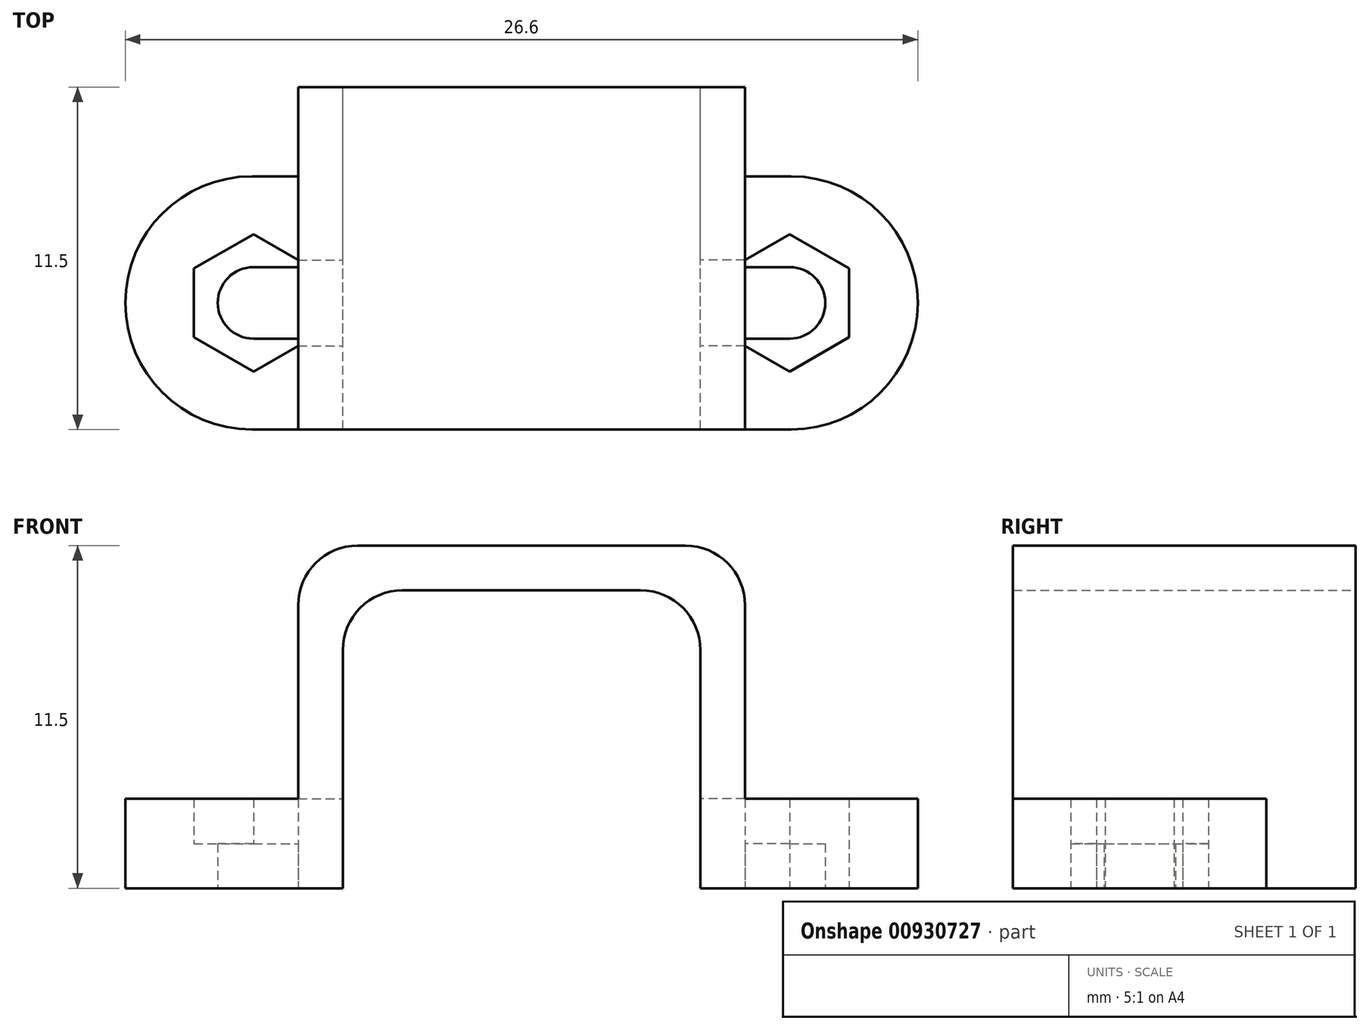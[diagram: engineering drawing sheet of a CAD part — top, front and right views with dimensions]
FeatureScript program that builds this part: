
annotation { "Feature Type Name" : "Feature", "Feature Type Description" : "" }
export const myFeature = defineFeature(function(context is Context, id is Id, definition is map)
    precondition{}
    {
        {
            var Q0;
            Q0=qCreatedBy(makeId("Top.planeOp"),FACE);
            var sketch = newSketch(context, id + "F0", { "sketchPlane" : qUnion([Q0])});
            skLineSegment(sketch, "E0", {"start": v(0, 0) * mm, "end": v(-9, 0) * mm, "construction": true});
            skArc(sketch, "E1", {"start": v(-9, 1.2) * mm, "mid": v(-10.2, 0) * mm, "end": v(-9, -1.2) * mm});
            skCircle(sketch, "E2.cCircle", {"center": v(-9, 0) * mm, "radius": 2 * mm, "construction": true});
            skLineSegment(sketch, "E2.2", {"start": v(-9, -2.3) * mm, "end": v(-11, -1.15) * mm});
            skLineSegment(sketch, "E2.3", {"start": v(-11, -1.15) * mm, "end": v(-11, 1.15) * mm});
            skLineSegment(sketch, "E2.4", {"start": v(-11, 1.15) * mm, "end": v(-9, 2.3) * mm});
            skLineSegment(sketch, "E2.5", {"start": v(-9, 2.3) * mm, "end": v(-7.5, 1.44) * mm});
            skPoint(sketch, "E2.0.midPoint", {"position": v(-7, 0) * mm});
            skLineSegment(sketch, "E3", {"start": v(0, -4.25) * mm, "end": v(-7.5, -4.25) * mm});
            skLineSegment(sketch, "E4", {"start": v(-7.5, -4.25) * mm, "end": v(-13.3, -4.25) * mm});
            skLineSegment(sketch, "E5", {"start": v(-13.3, -4.25) * mm, "end": v(-13.3, 4.25) * mm});
            skLineSegment(sketch, "E6", {"start": v(0, -4.25) * mm, "end": v(0, 7.25) * mm});
            skLineSegment(sketch, "E7", {"start": v(-7.5, -4.25) * mm, "end": v(-7.5, 7.25) * mm});
            skLineSegment(sketch, "E8", {"start": v(0, 7.25) * mm, "end": v(-7.5, 7.25) * mm});
            skLineSegment(sketch, "E9", {"start": v(-13.3, 4.25) * mm, "end": v(-7.5, 4.25) * mm});
            skLineSegment(sketch, "E10", {"start": v(-6, -4.25) * mm, "end": v(-6, 7.25) * mm});
            skPoint(sketch, "E11.trimOffspring.end.orphan", {"position": v(-7, 1.15) * mm});
            skLineSegment(sketch, "E12.trimOffspring", {"start": v(-7.5, -1.44) * mm, "end": v(-9, -2.3) * mm});
            skPoint(sketch, "E2.0.end.orphan", {"position": v(-7, -1.15) * mm});
            skPoint(sketch, "E13.start.orphan", {"position": v(-9, -1.2) * mm});
            skLineSegment(sketch, "E14", {"start": v(-7.5, 1.44) * mm, "end": v(-6, 1.44) * mm});
            skLineSegment(sketch, "E15", {"start": v(-7.5, -1.44) * mm, "end": v(-6, -1.44) * mm});
            skPoint(sketch, "E16.start.orphan", {"position": v(-9, 1.2) * mm});
            skLineSegment(sketch, "E17", {"start": v(-9, -1.2) * mm, "end": v(-7.5, -1.2) * mm});
            skLineSegment(sketch, "E18", {"start": v(-9, 1.2) * mm, "end": v(-7.5, 1.2) * mm});
            skLineSegment(sketch, "E19.MirrorCS", {"start": v(0, 7.25) * mm, "end": v(7.5, 7.25) * mm});
            skLineSegment(sketch, "E20.MirrorCS", {"start": v(0, -4.25) * mm, "end": v(7.5, -4.25) * mm});
            skLineSegment(sketch, "E21.MirrorCS", {"start": v(13.3, 4.25) * mm, "end": v(7.5, 4.25) * mm});
            skLineSegment(sketch, "E22.MirrorCS", {"start": v(6, -4.25) * mm, "end": v(6, 7.25) * mm});
            skLineSegment(sketch, "E23.MirrorCS", {"start": v(13.3, -4.25) * mm, "end": v(13.3, 4.25) * mm});
            skLineSegment(sketch, "E24.MirrorCS", {"start": v(7.5, -4.25) * mm, "end": v(13.3, -4.25) * mm});
            skLineSegment(sketch, "E25.MirrorCS", {"start": v(7.5, -4.25) * mm, "end": v(7.5, 7.25) * mm});
            skArc(sketch, "E26.MirrorCS", {"start": v(9, 1.2) * mm, "mid": v(10.2, 0) * mm, "end": v(9, -1.2) * mm});
            skLineSegment(sketch, "E27.MirrorCS", {"start": v(9, -1.2) * mm, "end": v(7.5, -1.2) * mm});
            skLineSegment(sketch, "E28.MirrorCS", {"start": v(9, 1.2) * mm, "end": v(7.5, 1.2) * mm});
            skLineSegment(sketch, "E29.MirrorCS", {"start": v(7.5, 1.44) * mm, "end": v(6, 1.44) * mm});
            skLineSegment(sketch, "E30.MirrorCS", {"start": v(7.5, -1.44) * mm, "end": v(6, -1.44) * mm});
            skLineSegment(sketch, "E31.MirrorCS", {"start": v(9, 2.3) * mm, "end": v(7.5, 1.44) * mm});
            skLineSegment(sketch, "E32.MirrorCS", {"start": v(11, 1.15) * mm, "end": v(9, 2.3) * mm});
            skLineSegment(sketch, "E33.MirrorCS", {"start": v(11, -1.15) * mm, "end": v(11, 1.15) * mm});
            skLineSegment(sketch, "E34.MirrorCS", {"start": v(9, -2.3) * mm, "end": v(11, -1.15) * mm});
            skLineSegment(sketch, "E35.MirrorCS", {"start": v(7.5, -1.44) * mm, "end": v(9, -2.3) * mm});
            skSolve(sketch);
        }
        {
            var Q0;
            {var subQ1=sQuery(id+"F0.wireOp",EDGE,"E6");Q0=makeQuery(id+"F0.imprint","IMPRINT",FACE,{"disambiguationData":[TD([[makeQuery(id+"F0.imprint","IMPRINT",EDGE,{"derivedFrom":subQ1}),1.0]])]});}
            var Q1;
            {var subQ3=sQuery(id+"F0.wireOp",EDGE,"E14");Q1=makeQuery(id+"F0.imprint","IMPRINT",FACE,{"disambiguationData":[TD([[makeQuery(id+"F0.imprint","IMPRINT",EDGE,{"derivedFrom":subQ3}),1.0]])]});}
            var Q2;
            {var subQ0=sQuery(id+"F0.wireOp",EDGE,"E14");Q2=makeQuery(id+"F0.imprint","IMPRINT",FACE,{"disambiguationData":[TD([[makeQuery(id+"F0.imprint","IMPRINT",EDGE,{"derivedFrom":subQ0}),-1.0]])]});}
            var Q3;
            {var subQ5=sQuery(id+"F0.wireOp",EDGE,"E15");Q3=makeQuery(id+"F0.imprint","IMPRINT",FACE,{"disambiguationData":[TD([[makeQuery(id+"F0.imprint","IMPRINT",EDGE,{"derivedFrom":subQ5}),-1.0]])]});}
            var Q4;
            {var subQ5=sQuery(id+"F0.wireOp",EDGE,"E6");Q4=makeQuery(id+"F0.imprint","IMPRINT",FACE,{"disambiguationData":[TD([[makeQuery(id+"F0.imprint","IMPRINT",EDGE,{"derivedFrom":subQ5}),-1.0]])]});}
            var Q5;
            {var subQ4=sQuery(id+"F0.wireOp",EDGE,"E29.MirrorCS");Q5=makeQuery(id+"F0.imprint","IMPRINT",FACE,{"disambiguationData":[TD([[makeQuery(id+"F0.imprint","IMPRINT",EDGE,{"derivedFrom":subQ4}),-1.0]])]});}
            var Q6;
            {var subQ4=sQuery(id+"F0.wireOp",EDGE,"E30.MirrorCS");Q6=makeQuery(id+"F0.imprint","IMPRINT",FACE,{"disambiguationData":[TD([[makeQuery(id+"F0.imprint","IMPRINT",EDGE,{"derivedFrom":subQ4}),-1.0]])]});}
            var Q7;
            {var subQ5=sQuery(id+"F0.wireOp",EDGE,"E30.MirrorCS");Q7=makeQuery(id+"F0.imprint","IMPRINT",FACE,{"disambiguationData":[TD([[makeQuery(id+"F0.imprint","IMPRINT",EDGE,{"derivedFrom":subQ5}),1.0]])]});}
            extrude(context, id + "F1", {"entities" : qUnion([Q0, Q1, Q2, Q3, Q4, Q5, Q6, Q7]), "depth" : 11.5 * mm, "offsetDistance" : 25 * mm});
        }
        {
            var Q0;
            {var subQ1=sQuery(id+"F0.wireOp",EDGE,"E6");Q0=makeQuery(id+"F0.imprint","IMPRINT",FACE,{"disambiguationData":[TD([[makeQuery(id+"F0.imprint","IMPRINT",EDGE,{"derivedFrom":subQ1}),1.0]])]});}
            var Q1;
            {var subQ5=sQuery(id+"F0.wireOp",EDGE,"E6");Q1=makeQuery(id+"F0.imprint","IMPRINT",FACE,{"disambiguationData":[TD([[makeQuery(id+"F0.imprint","IMPRINT",EDGE,{"derivedFrom":subQ5}),-1.0]])]});}
            extrude(context, id + "F2", {"entities" : qUnion([Q0, Q1]), "operationType" : NewBodyOperationType.REMOVE, "depth" : 10 * mm, "offsetDistance" : 25 * mm});
        }
        {
            var Q0;
            {var subQ0=sQuery(id+"F0.wireOp",EDGE,"E14");Q0=makeQuery(id+"F0.imprint","IMPRINT",FACE,{"disambiguationData":[TD([[makeQuery(id+"F0.imprint","IMPRINT",EDGE,{"derivedFrom":subQ0}),-1.0]])]});}
            var Q1;
            {var subQ4=sQuery(id+"F0.wireOp",EDGE,"E30.MirrorCS");Q1=makeQuery(id+"F0.imprint","IMPRINT",FACE,{"disambiguationData":[TD([[makeQuery(id+"F0.imprint","IMPRINT",EDGE,{"derivedFrom":subQ4}),-1.0]])]});}
            extrude(context, id + "F3", {"entities" : qUnion([Q0, Q1]), "operationType" : NewBodyOperationType.REMOVE, "depth" : 3 * mm, "offsetDistance" : 25 * mm});
        }
        {
            var Q0;
            Q0=makeQuery(id+"F0.imprint","IMPRINT",FACE,{"disambiguationData":[TD([[makeQuery(id+"F0.imprint","IMPRINT",EDGE,{"derivedFrom":sQuery(id+"F0.wireOp",EDGE,"E2.2")}),1.0]])]});
            var Q1;
            {var subQ4=sQuery(id+"F0.wireOp",EDGE,"E21.MirrorCS");Q1=makeQuery(id+"F0.imprint","IMPRINT",FACE,{"disambiguationData":[TD([[makeQuery(id+"F0.imprint","IMPRINT",EDGE,{"derivedFrom":subQ4}),1.0]])]});}
            extrude(context, id + "F4", {"entities" : qUnion([Q0, Q1]), "operationType" : NewBodyOperationType.ADD, "depth" : 3 * mm, "offsetDistance" : 25 * mm});
        }
        {
            var Q0;
            Q0=makeQuery(id+"F0.imprint","IMPRINT",FACE,{"disambiguationData":[TD([[makeQuery(id+"F0.imprint","IMPRINT",EDGE,{"derivedFrom":sQuery(id+"F0.wireOp",EDGE,"E1")}),-1.0]])]});
            var Q1;
            Q1=makeQuery(id+"F0.imprint","IMPRINT",FACE,{"disambiguationData":[TD([[makeQuery(id+"F0.imprint","IMPRINT",EDGE,{"derivedFrom":sQuery(id+"F0.wireOp",EDGE,"E26.MirrorCS")}),1.0]])]});
            extrude(context, id + "F5", {"entities" : qUnion([Q0, Q1]), "operationType" : NewBodyOperationType.ADD, "depth" : 1.5 * mm, "offsetDistance" : 25 * mm});
        }
        {
            var Q0;
            Q0=makeQuery(id+"F4.opExtrude","SWEPT_EDGE",EDGE,{"disambiguationData":[OSD([sQuery(id+"F0.wireOp",EDGE,"E4"),sQuery(id+"F0.wireOp",EDGE,"E5")])]});
            var Q1;
            Q1=makeQuery(id+"F4.opExtrude","SWEPT_EDGE",EDGE,{"disambiguationData":[OSD([sQuery(id+"F0.wireOp",EDGE,"E5"),sQuery(id+"F0.wireOp",EDGE,"E9")])]});
            var Q2;
            Q2=makeQuery(id+"F4.opExtrude","SWEPT_EDGE",EDGE,{"disambiguationData":[OSD([sQuery(id+"F0.wireOp",EDGE,"E21.MirrorCS"),sQuery(id+"F0.wireOp",EDGE,"E23.MirrorCS")])]});
            var Q3;
            Q3=makeQuery(id+"F4.opExtrude","SWEPT_EDGE",EDGE,{"disambiguationData":[OSD([sQuery(id+"F0.wireOp",EDGE,"E23.MirrorCS"),sQuery(id+"F0.wireOp",EDGE,"E24.MirrorCS")])]});
            fillet(context, id + "F6", {"entities" : qUnion([Q0, Q1, Q2, Q3]), "radius" : 4.25 * mm, "tangentPropagation" : true, "allowEdgeOverflow" : false});
        }
        {
            var Q0;
            Q0=makeQuery(id+"F2.boolean.opBoolean","COPY",EDGE,{"derivedFrom":makeQuery(id+"F2.opExtrude","CAP_EDGE",EDGE,{"disambiguationData":[OSD([sQuery(id+"F0.wireOp",EDGE,"E22.MirrorCS")])],"isStart":false})});
            var Q1;
            Q1=makeQuery(id+"F1.opExtrude","CAP_EDGE",EDGE,{"disambiguationData":[OSD([sQuery(id+"F0.wireOp",EDGE,"E25.MirrorCS")])],"isStart":false});
            var Q2;
            Q2=makeQuery(id+"F1.opExtrude","CAP_EDGE",EDGE,{"disambiguationData":[OSD([sQuery(id+"F0.wireOp",EDGE,"E7")])],"isStart":false});
            var Q3;
            Q3=makeQuery(id+"F2.boolean.opBoolean","COPY",EDGE,{"derivedFrom":makeQuery(id+"F2.opExtrude","CAP_EDGE",EDGE,{"disambiguationData":[OSD([sQuery(id+"F0.wireOp",EDGE,"E10")])],"isStart":false})});
            fillet(context, id + "F7", {"entities" : qUnion([Q0, Q1, Q2, Q3]), "radius" : 2 * mm, "tangentPropagation" : true, "allowEdgeOverflow" : false});
        }
    });
